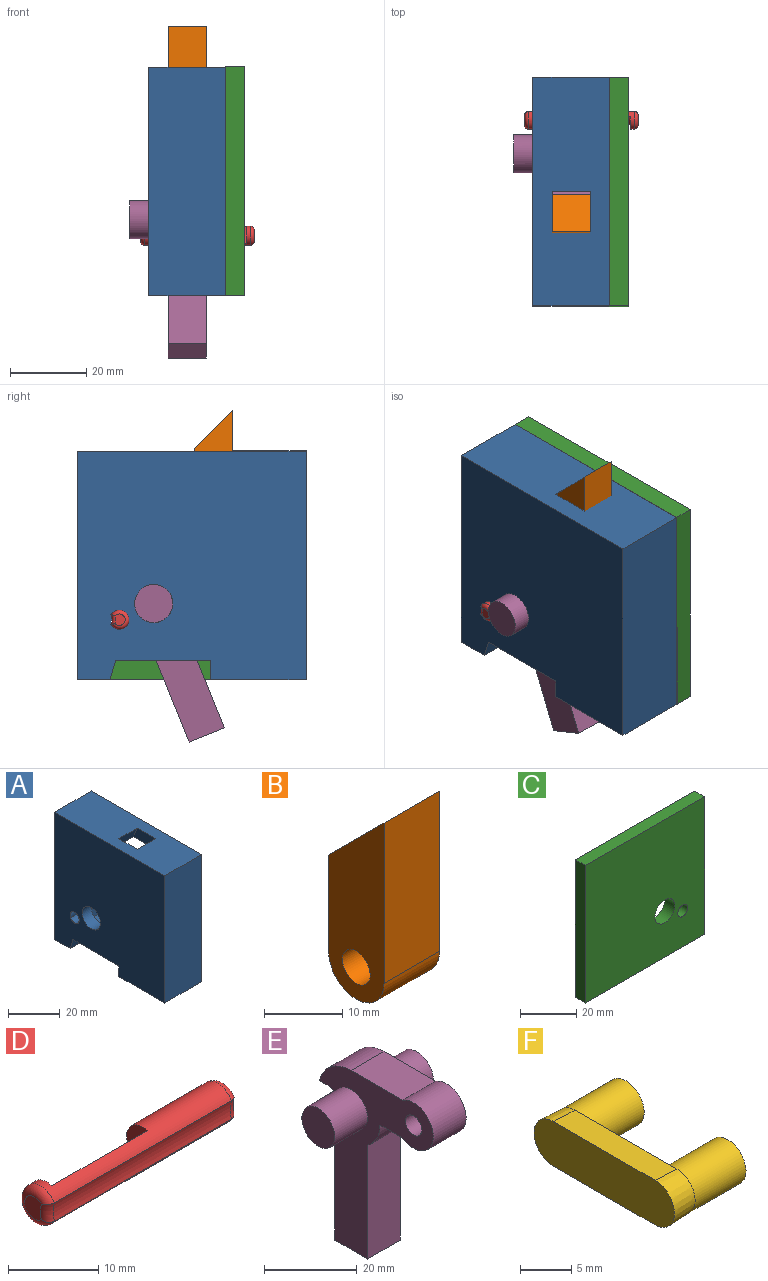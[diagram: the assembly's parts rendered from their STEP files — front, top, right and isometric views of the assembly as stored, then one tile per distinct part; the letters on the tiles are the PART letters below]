
ASSEMBLY  parts=6 mates=5
PART A: 25 faces, bbox 20x60x60 mm
  f0: cylinder r=2.5mm len=5mm, axis (-1,0,0), area 65.4mm2, adj f14,f17,f18
  f1: plane 60x20mm, normal (0,-1,0), area 1200mm2, adj f2,f12,f13,f14
  f2: plane 25x20mm, normal (0,0,-1), area 500mm2, adj f1,f3,f13,f14
  f3: plane 20x5mm, normal (0,1,0), area 100mm2, adj f2,f4,f13,f14,f15
  f4: plane 20x15mm, normal (0,0,1), area 300mm2, adj f3,f5,f13,f17
  f5: plane 50x15mm, normal (0,1,0), area 750mm2, adj f4,f6,f13,f17
  f6: plane 50x15mm, normal (0,0,-1), area 610mm2, adj f5,f7,f13,f17,f22,f23,f24
  f7: plane 50x15mm, normal (0,-1,0), area 652.3mm2, adj f6,f8,f13,f17,f18,f19
  f8: plane 15x5mm, normal (0,0,1), area 75mm2, adj f7,f9,f13,f17
  f9: plane 20x5mm, normal (0,-0.96,-0.29), area 104.4mm2, adj f8,f10,f13,f14,f15
  f10: plane 20x8.5mm, normal (0,0,-1), area 170mm2, adj f9,f11,f13,f14
  f11: plane 60x20mm, normal (0,1,0), area 1200mm2, adj f10,f12,f13,f14
  f12: plane 60x20mm, normal (0,0,1), area 1100mm2, adj f1,f11,f13,f14,f17,f22,f23,f24
  f13: plane 60x60mm, normal (1,0,0), area 971.3mm2, adj f1,f2,f3,f4,f5,f6,f7,f8
  f14: plane 60x60mm, normal (-1,0,0), area 3373.9mm2, adj f0,f1,f2,f3,f9,f10,f11,f12
  f15: plane 25x5mm, normal (0,0,-1), area 125mm2, adj f3,f9,f14,f17
  f16: cylinder r=5mm len=10mm, axis (-1,0,0), area 157.1mm2, adj f14,f17
  f17: plane 55x50mm, normal (1,0,0), area 2417.8mm2, adj f0,f4,f5,f6,f7,f8,f12,f15
  f18: cylinder r=5mm len=15mm, axis (-1,0,0), area 148.4mm2, adj f0,f7,f14,f17,f19
  f19: plane 9.77x3.94mm, normal (1,0,0), area 28.7mm2, adj f7,f18
  f20: cylinder r=2.27mm len=10mm, axis (-1,0,0), area 142.7mm2, adj f17,f21
  f21: plane 4.54x4.54mm, normal (1,0,0), area 16.2mm2, adj f20
  f22: plane 14x5mm, normal (-1,0,0), area 60mm2, adj f6,f12,f23,f24
  f23: plane 10x5mm, normal (0,-0.93,-0.37), area 53.9mm2, adj f6,f12,f17,f22
  f24: plane 10x5mm, normal (0,0.93,-0.37), area 53.9mm2, adj f6,f12,f17,f22
PART B: 7 faces, bbox 10x10x30 mm
  f0: plane 25x10mm, normal (0,-1,0), area 250mm2, adj f1,f4,f5,f6
  f1: cylinder r=5mm len=10mm, axis (-1,0,0), area 157.1mm2, adj f0,f2,f4,f5
  f2: plane 15x10mm, normal (0,1,0), area 150mm2, adj f1,f4,f5,f6
  f3: cylinder r=2.5mm len=10mm, axis (-1,0,0), area 157.1mm2, adj f4,f5
  f4: plane 30x10mm, normal (1,0,0), area 219.6mm2, adj f0,f1,f2,f3,f6
  f5: plane 30x10mm, normal (-1,0,0), area 219.6mm2, adj f0,f1,f2,f3,f6
  f6: plane 10x10mm, normal (0,0.71,0.71), area 141.4mm2, adj f0,f2,f4,f5
PART C: 8 faces, bbox 60x5x60 mm
  f0: plane 60x5mm, normal (0,0,-1), area 300mm2, adj f1,f5,f6,f7
  f1: plane 60x5mm, normal (1,0,0), area 300mm2, adj f0,f2,f6,f7
  f2: plane 60x5mm, normal (0,0,1), area 300mm2, adj f1,f5,f6,f7
  f3: cylinder r=5mm len=10mm, axis (0,1,0), area 157.1mm2, adj f6,f7
  f4: cylinder r=2.5mm len=5mm, axis (0,1,0), area 78.5mm2, adj f6,f7
  f5: plane 60x5mm, normal (-1,0,0), area 300mm2, adj f0,f2,f6,f7
  f6: plane 60x60mm, normal (0,-1,0), area 3501.8mm2, adj f0,f1,f2,f3,f4,f5
  f7: plane 60x60mm, normal (0,1,0), area 3501.8mm2, adj f0,f1,f2,f3,f4,f5
PART D: 11 faces, bbox 29.8x5x5.4 mm
  f0: cylinder r=5mm len=27.8mm, axis (-1,0,0), area 70.7mm2, adj f1,f4,f10
  f1: cylinder r=2.5mm len=27.8mm, axis (-1,0,0), area 255mm2, adj f0,f3,f5,f6,f7,f9
  f2: plane 3x2.59mm, normal (1,0,0), area 6.4mm2, adj f3,f4
  f3: torus R=1.5mm, axis (1,0,0), area 17.1mm2, adj f1,f2,f4
  f4: torus R=6mm, axis (1,0,0), area 3.8mm2, adj f0,f2,f3
  f5: cylinder r=10mm len=15mm, axis (-1,0,0), area 75.2mm2, adj f1,f6,f7
  f6: plane 4.62x3.27mm, normal (-1,0,0), area 9.3mm2, adj f1,f5
  f7: plane 4.62x3.27mm, normal (1,0,0), area 9.3mm2, adj f1,f5
  f8: plane 3x2.59mm, normal (-1,0,0), area 6.4mm2, adj f9,f10
  f9: torus R=1.5mm, axis (1,0,0), area 17.1mm2, adj f1,f8,f10
  f10: torus R=6mm, axis (1,0,0), area 3.8mm2, adj f0,f8,f9
PART E: 19 faces, bbox 30x34.7x48.2 mm
  f0: cylinder r=5mm len=30mm, axis (-1,0,0), area 653.7mm2, adj f1,f2,f3,f4,f17,f18
  f1: plane 10x10mm, normal (1,0,0), area 78.5mm2, adj f0
  f2: plane 10x10mm, normal (-1,0,0), area 78.5mm2, adj f0
  f3: cylinder r=2.5mm len=10mm, axis (-1,0,0), area 26.1mm2, adj f0,f7,f17,f18
  f4: cylinder r=2.5mm len=10mm, axis (-1,0,0), area 26.1mm2, adj f0,f8,f17,f18
  f5: plane 28.52x10mm, normal (0,1,0), area 285.2mm2, adj f6,f15,f17,f18
  f6: cylinder r=10mm len=10mm, axis (-1,0,0), area 79.5mm2, adj f5,f7,f17,f18
  f7: plane 10x2.68mm, normal (0,0,1), area 26.8mm2, adj f3,f6,f17,f18
  f8: plane 10x2.68mm, normal (0,0,-1), area 26.8mm2, adj f4,f9,f17,f18
  f9: cylinder r=10mm len=10mm, axis (-1,0,0), area 131.8mm2, adj f8,f10,f17,f18
  f10: plane 15.68x10mm, normal (0,0,1), area 156.8mm2, adj f9,f11,f17,f18
  f11: cylinder r=6mm len=12mm, axis (-1,0,0), area 258.8mm2, adj f10,f12,f17,f18
  f12: plane 10x6.93mm, normal (0,0,-1), area 69.3mm2, adj f11,f13,f17,f18
  f13: cylinder r=8.75mm len=10mm, axis (-1,0,0), area 84.2mm2, adj f12,f14,f17,f18
  f14: plane 30x10mm, normal (0,-1,0), area 300mm2, adj f13,f15,f17,f18
  f15: plane 10x10mm, normal (0,0,-1), area 100mm2, adj f5,f14,f17,f18
  f16: cylinder r=2.5mm len=10mm, axis (-1,0,0), area 157.1mm2, adj f17,f18
  f17: plane 48.18x34.68mm, normal (1,0,0), area 629.4mm2, adj f0,f3,f4,f5,f6,f7,f8,f9
  f18: plane 48.18x34.68mm, normal (-1,0,0), area 629.4mm2, adj f0,f3,f4,f5,f6,f7,f8,f9
PART F: 10 faces, bbox 10x19.3x5.3 mm
  f0: cylinder r=2.5mm len=7mm, axis (-1,0,0), area 110mm2, adj f1,f4,f5
  f1: plane 5x5mm, normal (1,0,0), area 19.6mm2, adj f0
  f2: cylinder r=2.5mm len=7mm, axis (-1,0,0), area 110mm2, adj f3,f4,f7
  f3: plane 5x5mm, normal (1,0,0), area 19.6mm2, adj f2
  f4: plane 14x5mm, normal (1,0,0), area 50.4mm2, adj f0,f2,f6,f8
  f5: cone r=2.5mm half-angle=3deg, axis (-1,0,0), area 24.3mm2, adj f0,f6,f8,f9
  f6: plane 14x3mm, normal (0.05,0,1), area 42.1mm2, adj f4,f5,f7,f9
  f7: cone r=2.5mm half-angle=3deg, axis (-1,0,0), area 24.3mm2, adj f2,f6,f8,f9
  f8: plane 14x3mm, normal (0.05,0,-1), area 42.1mm2, adj f4,f5,f7,f9
  f9: plane 19.31x5.31mm, normal (-1,0,0), area 96.6mm2, adj f5,f6,f7,f8
PLACE A t=(-71.6,19.02,-13.66)mm fixed
PLACE B rot(axis=(-1,0,0),1.1deg) t=(-66.6,-12.06,27.08)mm
PLACE C rot(axis=(0,0,1),90deg) t=(-51.6,18.92,-13.65)mm
PLACE D rot(axis=(0,0,1),180deg) t=(-36,20.01,-2.88)mm
PLACE E rot(axis=(-1,0,0),22deg) t=(-61.6,4.02,1.34)mm
PLACE F rot(axis=(0,-0.7,-0.72),180deg) t=(-56.6,-12.06,27.08)mm
MATE revolute C.f7 <-> A.f13  axis (-1,0,0) through (-51.6,24.02,41.34)mm
MATE revolute F.f0 <-> B.f3  axis (1,0,0) through (-56.6,-12.06,27.08)mm
MATE revolute F.f2 <-> E.f11  axis (-1,0,0) through (-56.6,-11.73,13.09)mm
MATE revolute E.f6 <-> A.f16  axis (-1,0,0) through (-66.6,4.02,1.34)mm
MATE slider A.f14 <-> D.f1  axis (-1,0,0) through (-71.6,13.01,-2.88)mm
